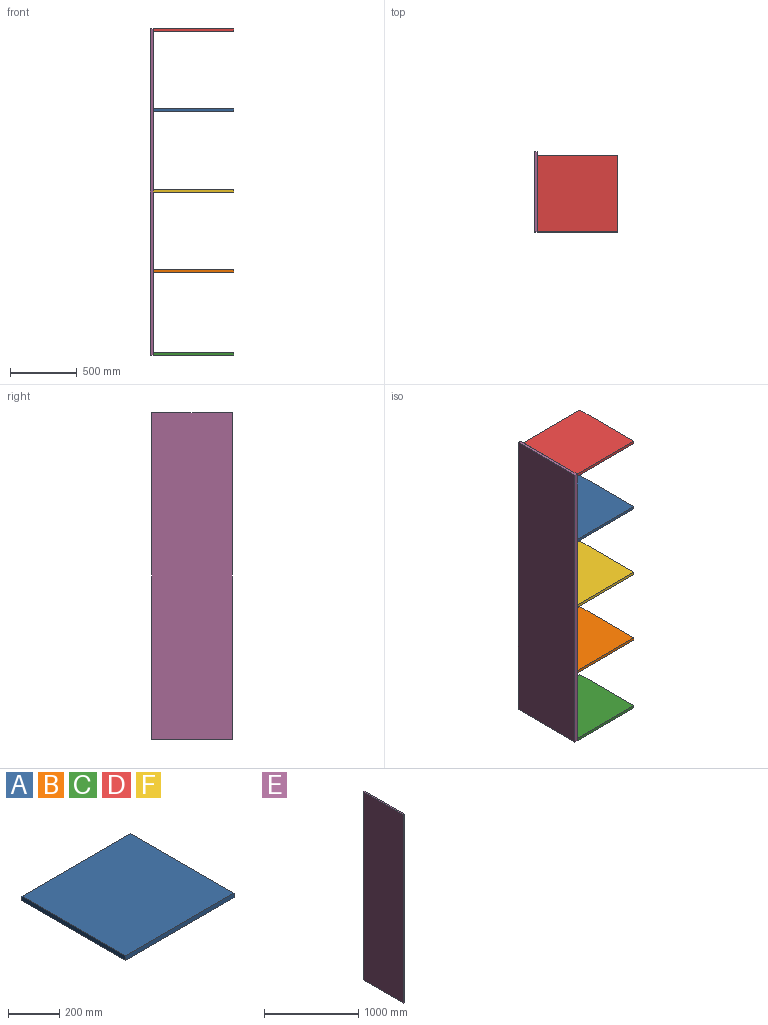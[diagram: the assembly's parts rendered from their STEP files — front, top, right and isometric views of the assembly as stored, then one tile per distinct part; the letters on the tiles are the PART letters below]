
ASSEMBLY  parts=6 mates=5
PART A: 6 faces, bbox 600x570x22 mm
  f0: plane 570x22mm, normal (-1,0,0), area 12540mm2, adj f1,f3,f4,f5
  f1: plane 600x22mm, normal (0,-1,0), area 13200mm2, adj f0,f2,f4,f5
  f2: plane 570x22mm, normal (1,0,0), area 12540mm2, adj f1,f3,f4,f5
  f3: plane 600x22mm, normal (0,1,0), area 13200mm2, adj f0,f2,f4,f5
  f4: plane 600x570mm, normal (0,0,1), area 342000mm2, adj f0,f1,f2,f3
  f5: plane 600x570mm, normal (0,0,-1), area 342000mm2, adj f0,f1,f2,f3
PART B: same geometry as A
PART C: same geometry as A
PART D: same geometry as A
PART E: 6 faces, bbox 22x600x2440 mm
  f0: plane 2440x22mm, normal (0,-1,0), area 53680mm2, adj f1,f3,f4,f5
  f1: plane 600x22mm, normal (0,0,-1), area 13200mm2, adj f0,f2,f4,f5
  f2: plane 2440x22mm, normal (0,1,0), area 53680mm2, adj f1,f3,f4,f5
  f3: plane 600x22mm, normal (0,0,1), area 13200mm2, adj f0,f2,f4,f5
  f4: plane 2440x600mm, normal (1,0,0), area 1464000mm2, adj f0,f1,f2,f3
  f5: plane 2440x600mm, normal (-1,0,0), area 1464000mm2, adj f0,f1,f2,f3
PART F: same geometry as A
PLACE A t=(109,0,1820)mm
PLACE B t=(109,0,620)mm
PLACE C t=(109,0,0)mm
PLACE D t=(109,0,2418)mm
PLACE E t=(87,0,0)mm
PLACE F t=(109,0,1220)mm
MATE fastened D.f0 <-> E.f4  axis (-1,0,0) through (109,0,2440)mm
MATE fastened B.f0 <-> E.f4  axis (-1,0,0) through (109,0,620)mm
MATE fastened A.f0 <-> E.f4  axis (-1,0,0) through (109,0,1820)mm
MATE fastened E.f4 <-> C.f0  axis (1,0,0) through (109,0,0)mm
MATE fastened F.f0 <-> E.f4  axis (-1,0,0) through (109,0,1220)mm
